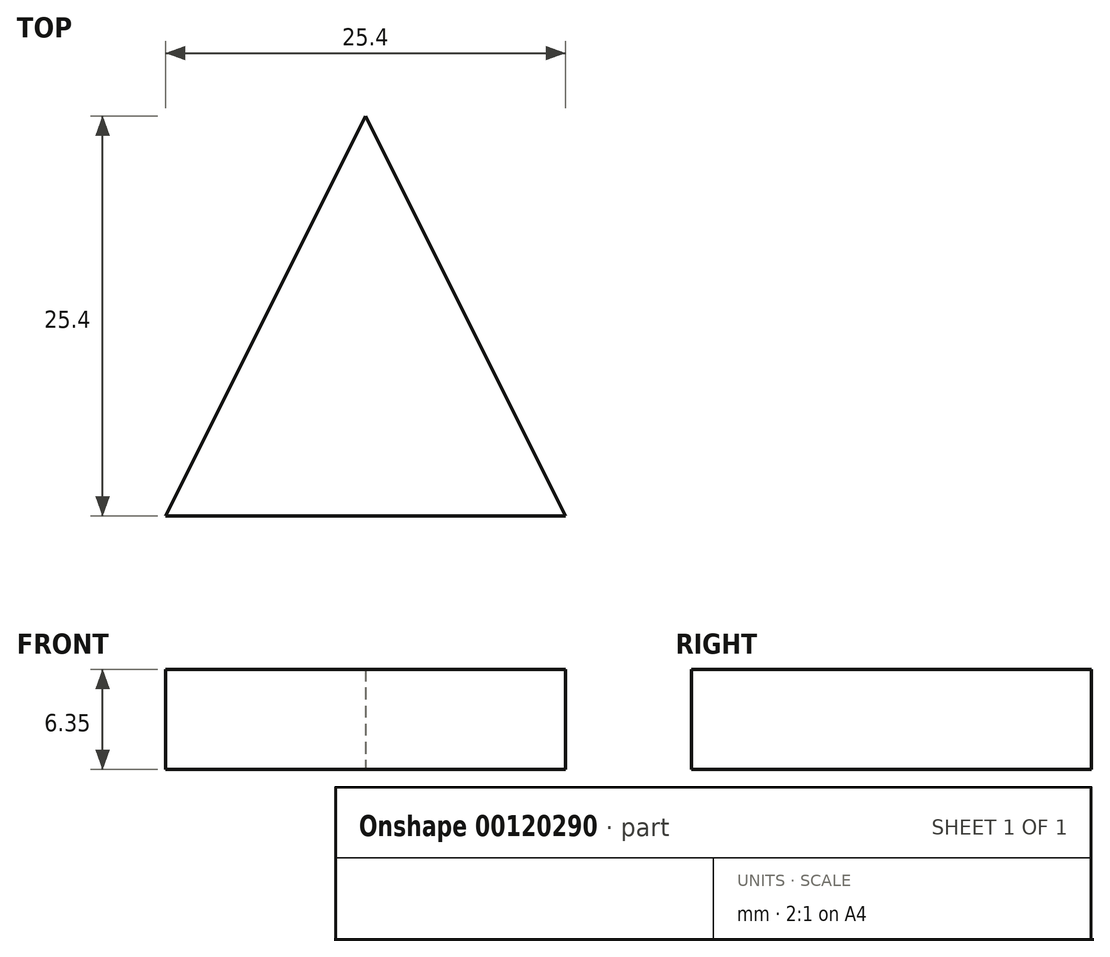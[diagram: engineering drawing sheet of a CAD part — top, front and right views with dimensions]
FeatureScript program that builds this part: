
annotation { "Feature Type Name" : "Feature", "Feature Type Description" : "" }
export const myFeature = defineFeature(function(context is Context, id is Id, definition is map)
    precondition{}
    {
        {
            var Q0;
            Q0=qCreatedBy(makeId("Top.planeOp"),FACE);
            var sketch = newSketch(context, id + "F0", { "sketchPlane" : qUnion([Q0])});
            skLineSegment(sketch, "E0", {"start": v(-12.7, 0) * mm, "end": v(12.7, 0) * mm});
            skLineSegment(sketch, "E1", {"start": v(0, 0) * mm, "end": v(0, 25.4) * mm, "construction": true});
            skLineSegment(sketch, "E2", {"start": v(-12.7, 0) * mm, "end": v(0, 25.4) * mm});
            skLineSegment(sketch, "E3", {"start": v(0, 25.4) * mm, "end": v(12.7, 0) * mm});
            skSolve(sketch);
        }
        {
            var Q0;
            Q0 = qSketchRegion(id + "F0", true);
            extrude(context, id + "F1", {"entities" : qUnion([Q0]), "depth" : 6.35 * mm});
        }
    });
